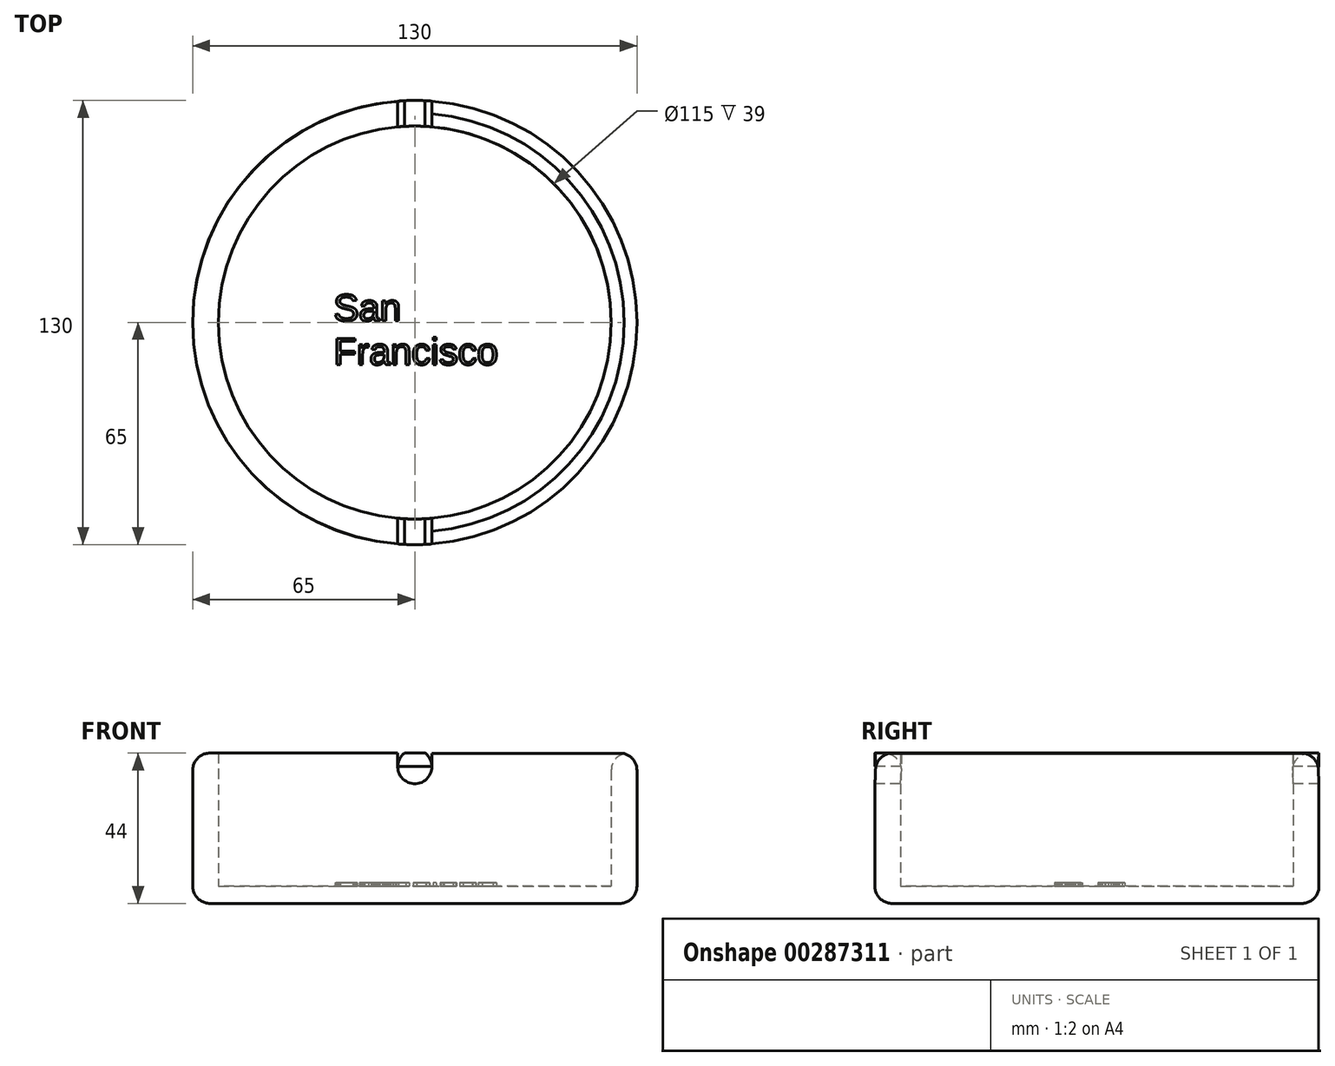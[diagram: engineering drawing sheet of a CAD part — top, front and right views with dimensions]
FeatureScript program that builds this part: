
annotation { "Feature Type Name" : "Feature", "Feature Type Description" : "" }
export const myFeature = defineFeature(function(context is Context, id is Id, definition is map)
    precondition{}
    {
        {
            var Q0;
            Q0=qCreatedBy(makeId("Top.planeOp"),FACE);
            var sketch = newSketch(context, id + "F0", { "sketchPlane" : qUnion([Q0])});
            skCircle(sketch, "E0", {"center": v(0, 0) * mm, "radius": 57.5 * mm});
            skCircle(sketch, "E1", {"center": v(0, 0) * mm, "radius": 65 * mm});
            skSolve(sketch);
        }
        {
            var Q0;
            Q0 = qSketchRegion(id + "F0", true);
            extrude(context, id + "F1", {"entities" : qUnion([Q0]), "depth" : 39 * mm});
        }
        {
            var Q0;
            Q0=makeQuery(id+"F1.opExtrude","CAP_FACE",FACE,{"disambiguationData":[OSD([sQuery(id+"F0.wireOp",EDGE,"E0"),sQuery(id+"F0.wireOp",EDGE,"E1")])],"isStart":true});
            var sketch = newSketch(context, id + "F2", { "sketchPlane" : qUnion([Q0])});
            skCircle(sketch, "E2", {"center": v(0, 0) * mm, "radius": 65 * mm});
            skSolve(sketch);
        }
        {
            var Q0;
            Q0 = qSketchRegion(id + "F2", true);
            extrude(context, id + "F3", {"entities" : qUnion([Q0]), "operationType" : NewBodyOperationType.ADD, "depth" : 5 * mm});
        }
        {
            var Q0;
            Q0=qCreatedBy(makeId("Front.planeOp"),FACE);
            var sketch = newSketch(context, id + "F4", { "sketchPlane" : qUnion([Q0])});
            skLineSegment(sketch, "E3", {"start": v(0, 35) * mm, "end": v(0, 0) * mm});
            skCircle(sketch, "E4", {"center": v(0, 35) * mm, "radius": 5 * mm});
            skLineSegment(sketch, "E5.bottom", {"start": v(5, 35.03) * mm, "end": v(-0.44, 35.03) * mm});
            skLineSegment(sketch, "E5.top", {"start": v(5, 39.98) * mm, "end": v(-0.44, 39.98) * mm});
            skLineSegment(sketch, "E5.left", {"start": v(5, 35.03) * mm, "end": v(5, 39.98) * mm});
            skLineSegment(sketch, "E6.MirrorCS", {"start": v(-5, 39.98) * mm, "end": v(0.44, 39.98) * mm});
            skLineSegment(sketch, "E7.MirrorCS", {"start": v(-5, 35.03) * mm, "end": v(-5, 39.98) * mm});
            skLineSegment(sketch, "E8.MirrorCS", {"start": v(-5, 35.03) * mm, "end": v(0.44, 35.03) * mm});
            skSolve(sketch);
        }
        {
            var Q0;
            {var subQ0=sQuery(id+"F4.wireOp",EDGE,"E4");var subQ1=makeQuery(id+"F4.imprint","INTERSECT",VERTEX,{"derivedFrom":[subQ0,sQuery(id+"F4.wireOp",EDGE,"WHB1GoVC-T0A8-ZOv6-8qDg-Df5qzJMjM2uo")]});Q0=makeQuery(id+"F4.imprint","IMPRINT",FACE,{"disambiguationData":[TD([[makeQuery(id+"F4.imprint","IMPRINT",EDGE,{"disambiguationData":[TD([[subQ1,-1.0]])],"derivedFrom":subQ0}),1.0]])]});}
            var Q1;
            {var subQ0=sQuery(id+"F4.wireOp",EDGE,"E7.MirrorCS");Q1=makeQuery(id+"F4.imprint","IMPRINT",FACE,{"disambiguationData":[TD([[makeQuery(id+"F4.imprint","IMPRINT",EDGE,{"derivedFrom":subQ0}),-1.0]])]});}
            var Q2;
            {var subQ2=sQuery(id+"F4.wireOp",EDGE,"E5.top");Q2=makeQuery(id+"F4.imprint","IMPRINT",FACE,{"disambiguationData":[TD([[makeQuery(id+"F4.imprint","IMPRINT",EDGE,{"derivedFrom":subQ2}),1.0]])]});}
            var Q3;
            {var subQ0=sQuery(id+"F4.wireOp",EDGE,"E5.bottom");Q3=makeQuery(id+"F4.imprint","IMPRINT",FACE,{"disambiguationData":[TD([[makeQuery(id+"F4.imprint","IMPRINT",EDGE,{"derivedFrom":subQ0}),1.0]])]});}
            extrude(context, id + "F5", {"entities" : qUnion([Q0, Q1, Q2, Q3]), "operationType" : NewBodyOperationType.REMOVE, "endBound" : BoundingType.SYMMETRIC, "oppositeDirection" : true, "depth" : 164.2 * mm});
        }
        {
            var Q0;
            {var subQ0=sQuery(id+"F0.wireOp",EDGE,"E1");Q0=makeQuery(id+"F5.boolean.opBoolean","SPLIT",EDGE,{"disambiguationData":[TD([makeQuery(id+"F5.opExtrude","SWEPT_FACE",FACE,{"disambiguationData":[OSD([sQuery(id+"F4.wireOp",EDGE,"E7.MirrorCS")])]})])],"derivedFrom":makeQuery(id+"F1.opExtrude","CAP_EDGE",EDGE,{"disambiguationData":[OSD([subQ0])],"isStart":false})});}
            var Q1;
            {var subQ0=sQuery(id+"F0.wireOp",EDGE,"E1");Q1=makeQuery(id+"F5.boolean.opBoolean","SPLIT",EDGE,{"disambiguationData":[TD([makeQuery(id+"F5.opExtrude","SWEPT_FACE",FACE,{"disambiguationData":[OSD([sQuery(id+"F4.wireOp",EDGE,"E5.left")])]})])],"derivedFrom":makeQuery(id+"F1.opExtrude","CAP_EDGE",EDGE,{"disambiguationData":[OSD([subQ0])],"isStart":false})});}
            var Q2;
            {var subQ0=sQuery(id+"F0.wireOp",EDGE,"E0");Q2=makeQuery(id+"F5.boolean.opBoolean","SPLIT",EDGE,{"disambiguationData":[TD([makeQuery(id+"F5.opExtrude","SWEPT_FACE",FACE,{"disambiguationData":[OSD([sQuery(id+"F4.wireOp",EDGE,"E5.left")])]})])],"derivedFrom":makeQuery(id+"F1.opExtrude","CAP_EDGE",EDGE,{"disambiguationData":[OSD([subQ0])],"isStart":false})});}
            var Q3;
            Q3=makeQuery(id+"F3.opExtrude","CAP_EDGE",EDGE,{"disambiguationData":[OSD([sQuery(id+"F2.wireOp",EDGE,"E2")])],"isStart":false});
            fillet(context, id + "F6", {"entities" : qUnion([Q0, Q1, Q2, Q3]), "radius" : 5 * mm, "tangentPropagation" : true, "allowEdgeOverflow" : false});
        }
        {
            var Q0;
            Q0=makeQuery(id+"F3.opExtrude","CAP_FACE",FACE,{"disambiguationData":[OSD([sQuery(id+"F2.wireOp",EDGE,"E2")])],"isStart":true});
            var sketch = newSketch(context, id + "F7", { "sketchPlane" : qUnion([Q0])});
            skText(sketch, "E9", { "text": "San \nFrancisco", "fontName": "Arimo-Regular.ttf"});
            const initialGuessF7  = {"E9": [-0.0238, 0.00047, 1, 0, 0.008]};
            skSetInitialGuess(sketch, initialGuessF7);
            skSolve(sketch);
        }
        {
            var Q0;
            Q0 = qSketchRegion(id + "F7", true);
            extrude(context, id + "F8", {"entities" : qUnion([Q0]), "operationType" : NewBodyOperationType.ADD, "depth" : 1 * mm});
        }
    });
